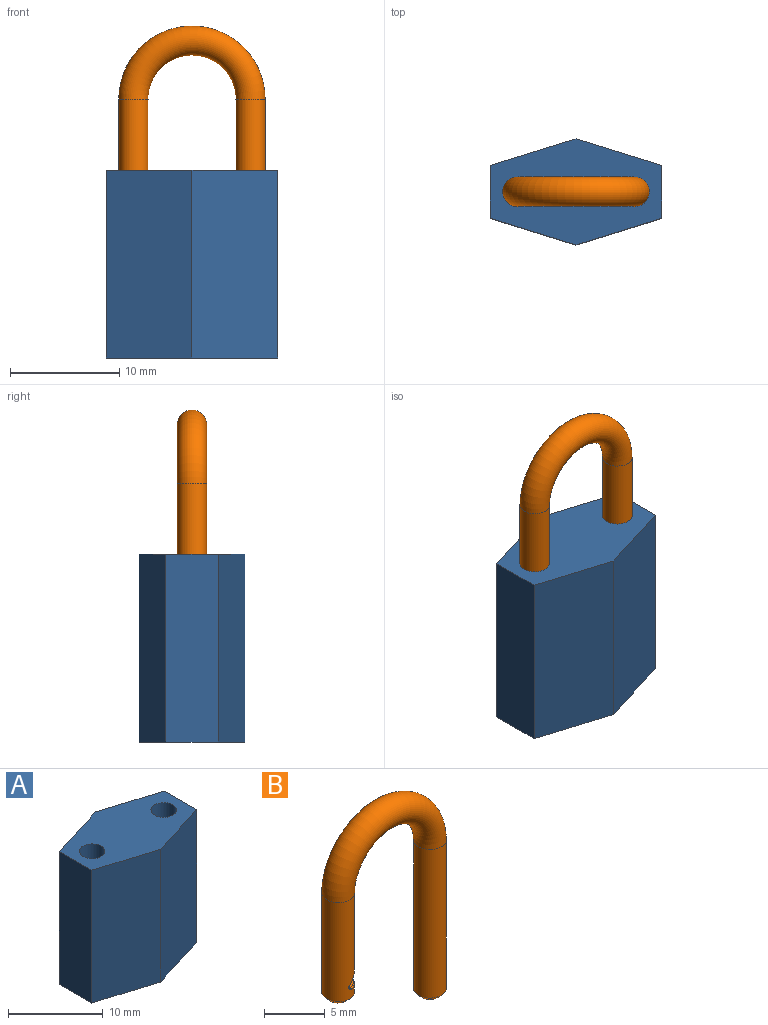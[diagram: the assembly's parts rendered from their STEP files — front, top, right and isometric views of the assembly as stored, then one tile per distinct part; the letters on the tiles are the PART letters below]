
ASSEMBLY  parts=2 mates=1
PART A: 12 faces, bbox 15.7x9.7x17.2 mm
  f0: plane 15.7x9.7mm, normal (0,0,1), area 102.8mm2, adj f1,f3,f4,f5,f6,f7,f8,f10
  f1: plane 17.2x4.85mm, normal (1,0,0), area 83.4mm2, adj f0,f2,f6,f7
  f2: plane 15.7x9.7mm, normal (0,0,-1), area 114.2mm2, adj f1,f3,f4,f5,f6,f7
  f3: plane 17.2x4.85mm, normal (-1,0,0), area 83.4mm2, adj f0,f2,f4,f5
  f4: plane 17.2x7.85mm, normal (-0.3,-0.96,0), area 141.3mm2, adj f0,f2,f3,f6
  f5: plane 17.2x7.85mm, normal (-0.3,0.96,0), area 141.3mm2, adj f0,f2,f3,f7
  f6: plane 17.2x7.85mm, normal (0.3,-0.96,0), area 141.3mm2, adj f0,f1,f2,f4
  f7: plane 17.2x7.85mm, normal (0.3,0.96,0), area 141.3mm2, adj f0,f1,f2,f5
  f8: cylinder r=1.35mm len=15.2mm, axis (0,0,1), area 128.9mm2, adj f0,f9
  f9: plane 2.7x2.7mm, normal (0,0,1), area 5.7mm2, adj f8
  f10: cylinder r=1.35mm len=7mm, axis (0,0,1), area 59.4mm2, adj f0,f11
  f11: plane 2.7x2.7mm, normal (0,0,1), area 5.7mm2, adj f10
PART B: 14 faces, bbox 14.5x2.9x22.8 mm
  f0: plane 1.7x1.7mm, normal (0,0,-1), area 2.3mm2, adj f6
  f1: plane 1.7x1.7mm, normal (0,0,-1), area 2.3mm2, adj f5
  f2: cylinder r=1.35mm len=15mm, axis (0,0,1), area 127.2mm2, adj f3,f6
  f3: torus R=5.35mm, axis (0,-1,0), area 142.6mm2, adj f2,f4
  f4: cylinder r=1.35mm len=10mm, axis (0,0,-1), area 79.1mm2, adj f3,f5,f10,f11,f12,f13
  f5: cone r=0.85mm half-angle=45deg, axis (0,0,1), area 4.9mm2, adj f1,f4
  f6: cone r=1.35mm half-angle=45deg, axis (0,0,1), area 4.9mm2, adj f0,f2
  f7: plane 2.5x1.27mm, normal (0.71,0,-0.71), area 3.5mm2, adj f9,f13
  f8: plane 2.47x1.06mm, normal (0,0,1), area 2mm2, adj f9,f10
  f9: cylinder r=0.2mm len=2.5mm, axis (0,1,0), area 1.2mm2, adj f7,f8,f11,f12
  f10: torus R=1.25mm, axis (0,0,-1), area 0.6mm2, adj f4,f8,f11,f12
  f11: bspline ~0.52x0.4mm, area 0.1mm2, adj f4,f9,f10,f13
  f12: bspline ~0.55x0.4mm, area 0.1mm2, adj f4,f9,f10,f13
  f13: bspline ~2.7x1.37mm, area 0.6mm2, adj f4,f7,f11,f12
PLACE A t=(9.86,0.35,0.59)mm fixed
PLACE B rot(axis=(0,0,-1),0deg) t=(9.86,0.35,0.59)mm
MATE cylindrical B.f2 <-> A.f8  axis (0,0,1) through (15.21,0.35,0.59)mm
